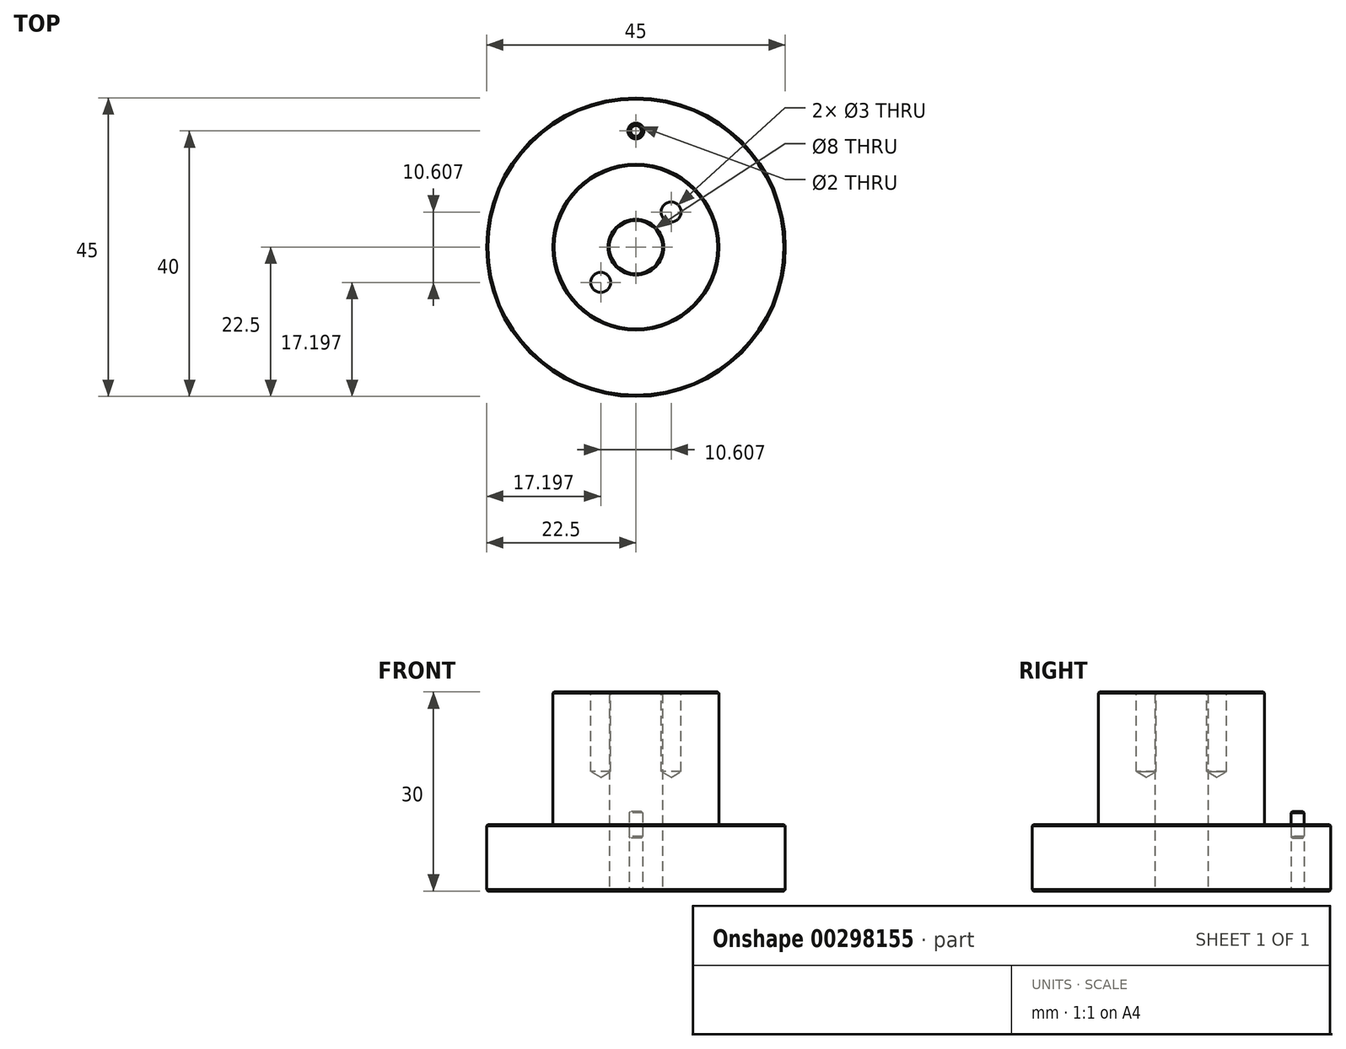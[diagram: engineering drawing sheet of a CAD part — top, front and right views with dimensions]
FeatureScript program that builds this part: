
annotation { "Feature Type Name" : "Feature", "Feature Type Description" : "" }
export const myFeature = defineFeature(function(context is Context, id is Id, definition is map)
    precondition{}
    {
        {
            var Q0;
            Q0=qCreatedBy(makeId("Top.planeOp"),FACE);
            var sketch = newSketch(context, id + "F0", { "sketchPlane" : qUnion([Q0])});
            skCircle(sketch, "E0", {"center": v(0, 0) * mm, "radius": 4 * mm});
            skCircle(sketch, "E1", {"center": v(0, 0) * mm, "radius": 12.5 * mm});
            skCircle(sketch, "E2", {"center": v(0, 0) * mm, "radius": 22.5 * mm});
            skCircle(sketch, "E3", {"center": v(0, 17.5) * mm, "radius": 1 * mm});
            skSolve(sketch);
        }
        {
            var Q0;
            Q0=makeQuery(id+"F0.imprint","IMPRINT",FACE,{"disambiguationData":[TD([[makeQuery(id+"F0.imprint","IMPRINT",EDGE,{"derivedFrom":sQuery(id+"F0.wireOp",EDGE,"E0")}),-1.0]])]});
            extrude(context, id + "F1", {"entities" : qUnion([Q0]), "depth" : 30 * mm});
        }
        {
            var Q0;
            Q0=makeQuery(id+"F0.imprint","IMPRINT",FACE,{"disambiguationData":[TD([[makeQuery(id+"F0.imprint","IMPRINT",EDGE,{"derivedFrom":sQuery(id+"F0.wireOp",EDGE,"E1")}),-1.0]])]});
            extrude(context, id + "F2", {"entities" : qUnion([Q0]), "operationType" : NewBodyOperationType.ADD, "depth" : 10 * mm});
        }
        {
            var Q0;
            Q0=makeQuery(id+"F2.opExtrude","CAP_FACE",FACE,{"disambiguationData":[OSD([sQuery(id+"F0.wireOp",EDGE,"E1"),sQuery(id+"F0.wireOp",EDGE,"E2"),sQuery(id+"F0.wireOp",EDGE,"E3")])],"isStart":false});
            var sketch = newSketch(context, id + "F3", { "sketchPlane" : qUnion([Q0])});
            skCircle(sketch, "E4", {"center": v(0, 17.5) * mm, "radius": 1 * mm});
            skSolve(sketch);
        }
        {
            var Q0;
            Q0=makeQuery(id+"F3.imprint","IMPRINT",FACE,{"disambiguationData":[TD([[makeQuery(id+"F3.imprint","IMPRINT",EDGE,{"derivedFrom":sQuery(id+"F3.wireOp",EDGE,"E4")}),1.0]])]});
            extrude(context, id + "F4", {"entities" : qUnion([Q0]), "endBound" : BoundingType.SYMMETRIC, "depth" : 4 * mm});
        }
        {
            var Q0;
            Q0=makeQuery(id+"F4.opExtrude","CAP_FACE",FACE,{"disambiguationData":[OSD([sQuery(id+"F3.wireOp",EDGE,"E4")])],"isStart":false});
            var Q1;
            Q1=makeQuery(id+"F4.opExtrude","CAP_EDGE",EDGE,{"disambiguationData":[OSD([sQuery(id+"F3.wireOp",EDGE,"E4")])],"isStart":true});
            chamfer(context, id + "F5", {"entities" : qUnion([Q0, Q1]), "width" : 0.2 * mm, "tangentPropagation" : true});
        }
        {
            var Q0;
            Q0=makeQuery(id+"F1.opExtrude","CAP_EDGE",EDGE,{"disambiguationData":[OSD([sQuery(id+"F0.wireOp",EDGE,"E1")])],"isStart":false});
            var Q1;
            Q1=makeQuery(id+"F1.opExtrude","CAP_EDGE",EDGE,{"disambiguationData":[OSD([sQuery(id+"F0.wireOp",EDGE,"E0")])],"isStart":false});
            var Q2;
            Q2=makeQuery(id+"F2.opExtrude","CAP_EDGE",EDGE,{"disambiguationData":[OSD([sQuery(id+"F0.wireOp",EDGE,"E2")])],"isStart":false});
            var Q3;
            Q3=makeQuery(id+"F1.opExtrude","CAP_EDGE",EDGE,{"disambiguationData":[OSD([sQuery(id+"F0.wireOp",EDGE,"E0")])],"isStart":true});
            var Q4;
            Q4=makeQuery(id+"F2.opExtrude","CAP_EDGE",EDGE,{"disambiguationData":[OSD([sQuery(id+"F0.wireOp",EDGE,"E3")])],"isStart":true});
            var Q5;
            Q5=makeQuery(id+"F2.opExtrude","CAP_EDGE",EDGE,{"disambiguationData":[OSD([sQuery(id+"F0.wireOp",EDGE,"E3")])],"isStart":false});
            var Q6;
            Q6=makeQuery(id+"F2.opExtrude","CAP_EDGE",EDGE,{"disambiguationData":[OSD([sQuery(id+"F0.wireOp",EDGE,"E2")])],"isStart":true});
            chamfer(context, id + "F6", {"entities" : qUnion([Q0, Q1, Q2, Q3, Q4, Q5, Q6]), "width" : 0.2 * mm, "tangentPropagation" : true});
        }
        {
            var Q0;
            Q0=makeQuery(id+"F1.opExtrude","CAP_FACE",FACE,{"disambiguationData":[OSD([sQuery(id+"F0.wireOp",EDGE,"E0"),sQuery(id+"F0.wireOp",EDGE,"E1")])],"isStart":false});
            var sketch = newSketch(context, id + "F7", { "sketchPlane" : qUnion([Q0])});
            skCircle(sketch, "E5", {"center": v(-5.3, -5.3) * mm, "radius": 1.5 * mm});
            skLineSegment(sketch, "E6", {"start": v(0, 0) * mm, "end": v(0, -5.3) * mm});
            skLineSegment(sketch, "E7", {"start": v(0, -5.3) * mm, "end": v(-5.3, -5.3) * mm});
            skCircle(sketch, "E8.1.0", {"center": v(5.3, 5.3) * mm, "radius": 1.5 * mm});
            skPoint(sketch, "E8.center", {"position": v(0, 0) * mm});
            skLineSegment(sketch, "E8.anchor1", {"start": v(0, 0) * mm, "end": v(-5.3, -5.3) * mm, "construction": true});
            skLineSegment(sketch, "E8.anchor2", {"start": v(0, 0) * mm, "end": v(5.3, 5.3) * mm, "construction": true});
            skSolve(sketch);
        }
        {
            var Q0;
            Q0=sQuery(id+"F7.wireOp",VERTEX,"E8.1.0.center");
            var Q1;
            Q1=sQuery(id+"F7.wireOp",VERTEX,"E5.center");
            var Q2;
            Q2=makeQuery(id+"F1.opExtrude","SWEPT_BODY",BODY,{"disambiguationData":[OSD([sQuery(id+"F0.wireOp",EDGE,"E0"),sQuery(id+"F0.wireOp",EDGE,"E1")])]});
            hole(context, id + "F8", {"style" : HoleStyle.SIMPLE, "endStyle" : HoleEndStyle.BLIND, "holeDiameter" : 3 * mm, "holeDepth" : 12 * mm, "tappedDepth" : 12 * mm, "tapClearance" : 3, "locations" : qUnion([Q0, Q1]), "scope" : qUnion([Q2])});
        }
    });
